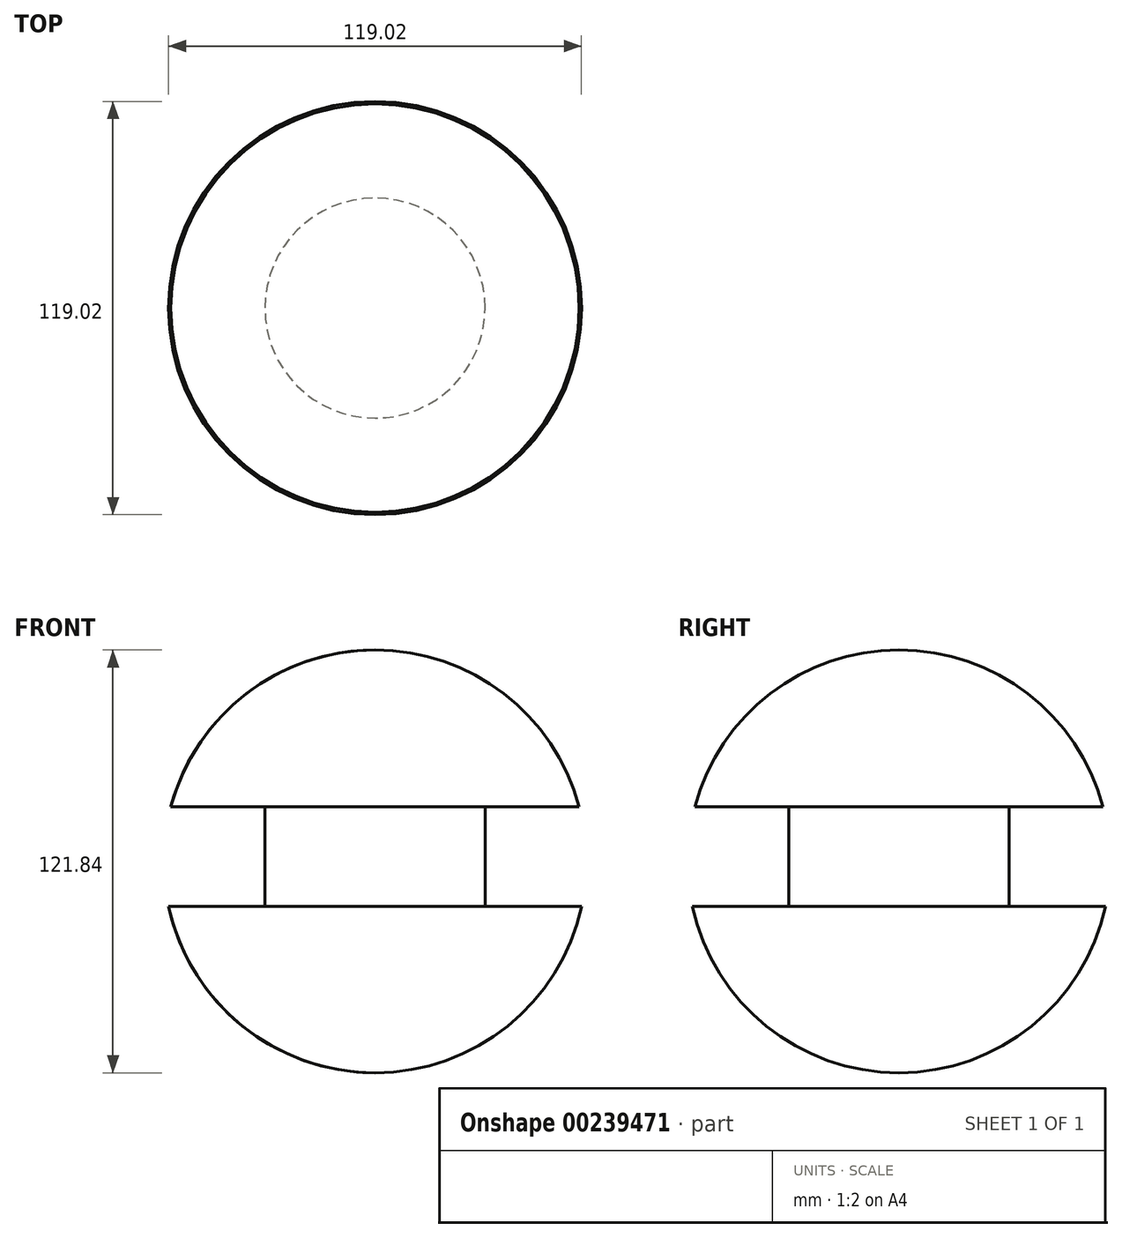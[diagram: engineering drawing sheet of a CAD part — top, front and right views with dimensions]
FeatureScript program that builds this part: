
annotation { "Feature Type Name" : "Feature", "Feature Type Description" : "" }
export const myFeature = defineFeature(function(context is Context, id is Id, definition is map)
    precondition{}
    {
        {
            var Q0;
            Q0=qCreatedBy(makeId("Front.planeOp"),FACE);
            var sketch = newSketch(context, id + "F0", { "sketchPlane" : qUnion([Q0])});
            skArc(sketch, "E0", {"start": v(0, -60.92) * mm, "mid": v(60.92, 0) * mm, "end": v(0, 60.92) * mm});
            skLineSegment(sketch, "E1", {"start": v(0, 60.92) * mm, "end": v(0, -60.92) * mm});
            skSolve(sketch);
        }
        {
            var Q0;
            Q0 = qSketchRegion(id + "F0", true);
            var Q1;
            Q1=sQuery(id+"F0.wireOp",EDGE,"E1");
            revolve(context, id + "F1", {"entities" : qUnion([Q0]), "axis" : qUnion([Q1]), "revolveType" : RevolveType.FULL});
        }
        {
            var Q0;
            Q0=qCreatedBy(makeId("Right.planeOp"),FACE);
            var sketch = newSketch(context, id + "F2", { "sketchPlane" : qUnion([Q0])});
            skLineSegment(sketch, "E2.bottom", {"start": v(-31.73, 15.77) * mm, "end": v(-86.96, 15.77) * mm});
            skLineSegment(sketch, "E2.top", {"start": v(-31.73, -13.02) * mm, "end": v(-86.96, -13.02) * mm});
            skLineSegment(sketch, "E2.left", {"start": v(-31.73, 15.77) * mm, "end": v(-31.73, -13.02) * mm});
            skLineSegment(sketch, "E2.right", {"start": v(-86.96, 15.77) * mm, "end": v(-86.96, -13.02) * mm});
            skLineSegment(sketch, "E3", {"start": v(0, 61.8) * mm, "end": v(0, -62.58) * mm, "construction": true});
            skSolve(sketch);
        }
        {
            var Q0;
            Q0 = qSketchRegion(id + "F2", true);
            var Q1;
            Q1=sQuery(id+"F2.wireOp",EDGE,"E3");
            revolve(context, id + "F3", {"operationType" : NewBodyOperationType.REMOVE, "entities" : qUnion([Q0]), "axis" : qUnion([Q1]), "revolveType" : RevolveType.FULL, "oppositeDirection" : true});
        }
    });
